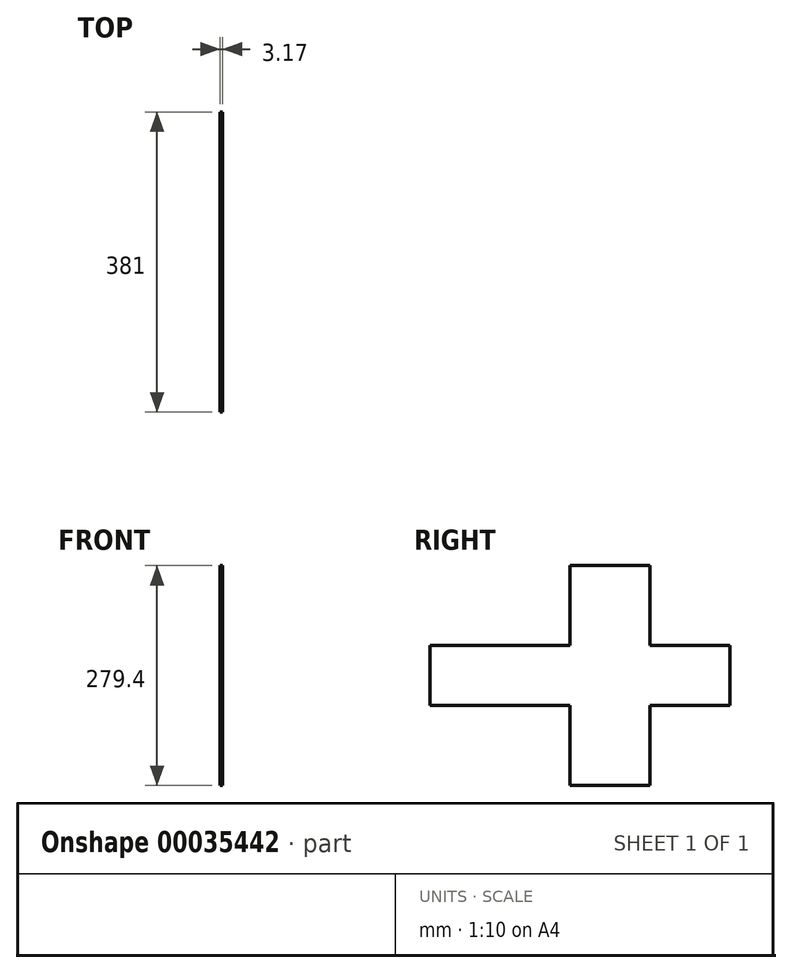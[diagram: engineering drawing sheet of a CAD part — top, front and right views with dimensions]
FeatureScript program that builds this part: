
annotation { "Feature Type Name" : "Feature", "Feature Type Description" : "" }
export const myFeature = defineFeature(function(context is Context, id is Id, definition is map)
    precondition{}
    {
        {
            var Q0;
            Q0=qCreatedBy(makeId("Right.planeOp"),FACE);
            var sketch = newSketch(context, id + "F0", { "sketchPlane" : qUnion([Q0])});
            skLineSegment(sketch, "E0", {"start": v(9.16, -76) * mm, "end": v(-92.44, -76) * mm});
            skLineSegment(sketch, "E1", {"start": v(-92.44, -76) * mm, "end": v(-92.44, -177.6) * mm});
            skLineSegment(sketch, "E2", {"start": v(-92.44, -177.6) * mm, "end": v(-194.04, -177.6) * mm});
            skLineSegment(sketch, "E3", {"start": v(-194.04, -177.6) * mm, "end": v(-194.04, -76) * mm});
            skLineSegment(sketch, "E4", {"start": v(-194.04, -76) * mm, "end": v(-295.64, -76) * mm});
            skLineSegment(sketch, "E5", {"start": v(-295.64, -76) * mm, "end": v(-295.64, 0.2) * mm});
            skLineSegment(sketch, "E6", {"start": v(-295.64, 0.2) * mm, "end": v(-194.04, 0.2) * mm});
            skLineSegment(sketch, "E7", {"start": v(-194.04, 0.2) * mm, "end": v(-194.04, 101.8) * mm});
            skLineSegment(sketch, "E8", {"start": v(-194.04, 101.8) * mm, "end": v(-92.44, 101.8) * mm});
            skLineSegment(sketch, "E9", {"start": v(-92.44, 101.8) * mm, "end": v(-92.44, 0.2) * mm});
            skLineSegment(sketch, "E10", {"start": v(-92.44, 0.2) * mm, "end": v(9.16, 0.2) * mm});
            skLineSegment(sketch, "E11", {"start": v(9.16, 0.2) * mm, "end": v(-92.44, 0.2) * mm});
            skLineSegment(sketch, "E12", {"start": v(-92.44, -76) * mm, "end": v(-92.44, 0.2) * mm});
            skLineSegment(sketch, "E13", {"start": v(-194.04, -76) * mm, "end": v(-194.04, 0.2) * mm});
            skLineSegment(sketch, "E14", {"start": v(-194.04, 0.2) * mm, "end": v(-194.04, -76) * mm});
            skLineSegment(sketch, "E15", {"start": v(-92.44, -76) * mm, "end": v(-194.04, -76) * mm});
            skLineSegment(sketch, "E16", {"start": v(-92.44, 0.2) * mm, "end": v(-194.04, 0.2) * mm});
            skLineSegment(sketch, "E17", {"start": v(85.08, -76) * mm, "end": v(85.08, 0.2) * mm});
            skLineSegment(sketch, "E18", {"start": v(9.16, -76) * mm, "end": v(9.16, 0.2) * mm});
            skLineSegment(sketch, "E19", {"start": v(-295.64, 0.2) * mm, "end": v(-295.64, -76) * mm});
            skLineSegment(sketch, "E20.bottom", {"start": v(-295.64, -76) * mm, "end": v(-371.84, -76) * mm});
            skLineSegment(sketch, "E20.top", {"start": v(-295.64, 0) * mm, "end": v(-371.84, 0) * mm});
            skLineSegment(sketch, "E20.left", {"start": v(-295.64, -76) * mm, "end": v(-295.64, 0) * mm});
            skLineSegment(sketch, "E20.right", {"start": v(-371.84, -76) * mm, "end": v(-371.84, 0) * mm});
            skSolve(sketch);
        }
        {
            var Q0;
            Q0 = qSketchRegion(id + "F0", true);
            extrude(context, id + "F1", {"entities" : qUnion([Q0]), "depth" : 3.17 * mm});
        }
    });
